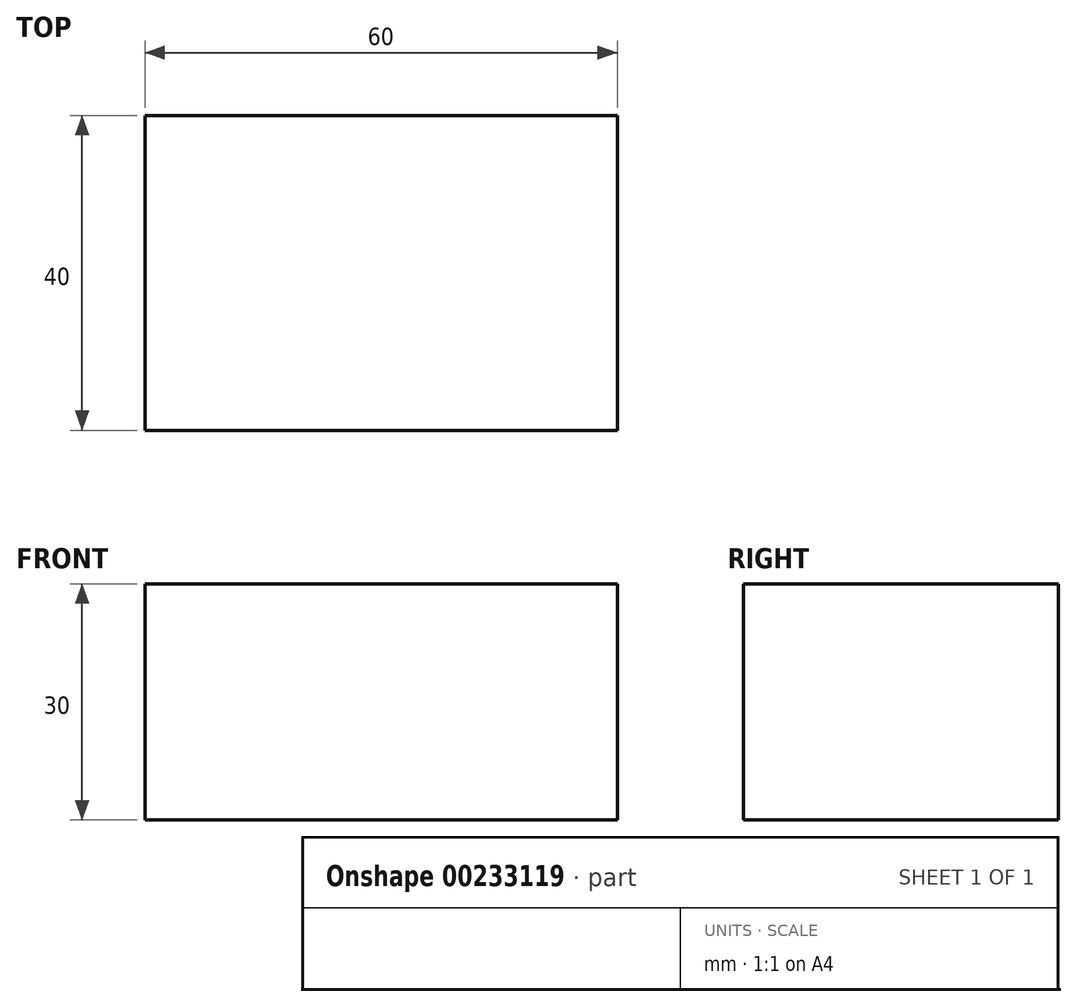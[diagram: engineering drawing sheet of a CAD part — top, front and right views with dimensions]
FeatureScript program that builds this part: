
annotation { "Feature Type Name" : "Feature", "Feature Type Description" : "" }
export const myFeature = defineFeature(function(context is Context, id is Id, definition is map)
    precondition{}
    {
        {
            var Q0;
            Q0=qCreatedBy(makeId("Right.planeOp"),FACE);
            var sketch = newSketch(context, id + "F0", { "sketchPlane" : qUnion([Q0])});
            skLineSegment(sketch, "E0.bottom", {"start": v(0, 0) * mm, "end": v(40, 0) * mm});
            skLineSegment(sketch, "E0.top", {"start": v(0, 30) * mm, "end": v(40, 30) * mm});
            skLineSegment(sketch, "E0.left", {"start": v(0, 0) * mm, "end": v(0, 30) * mm});
            skLineSegment(sketch, "E0.right", {"start": v(40, 0) * mm, "end": v(40, 30) * mm});
            skSolve(sketch);
        }
        {
            var Q0;
            Q0 = qSketchRegion(id + "F0", true);
            extrude(context, id + "F1", {"entities" : qUnion([Q0]), "depth" : 60 * mm});
        }
    });
